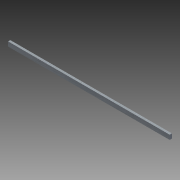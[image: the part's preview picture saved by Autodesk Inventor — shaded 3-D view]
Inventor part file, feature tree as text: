
AUTODESK INVENTOR PART (.ipt)
format: ipt  version: 2011 SP1 (Build 150282100, 282)  size: 70,144 bytes
history: native  units: in
note: dims shown in document units (in); Inventor stores cm internally (conversion verified against a paired STEP export)
features: extrude x1, sketch x1
ambient origin geometry x8: Origin, YZ Plane, XZ Plane, XY Plane, X Axis, Y Axis, Z Axis, Center Point
bodies: Solid1 (feature_tree)
feature tree (2):
  extrude  "Extrusion1"  Depth=0.125in
  sketch  "Sketch1"  dims[d0=0.25in d1=0.125in d2=9.0in d3=4.5in d4=0.125in d5=0.0in]
